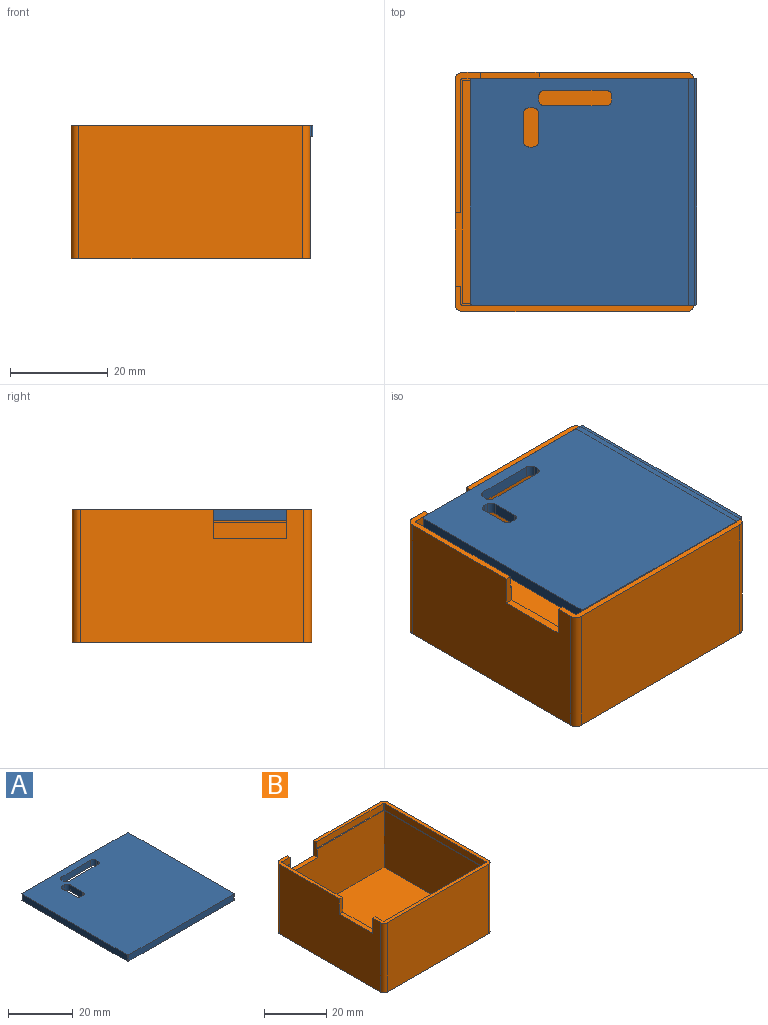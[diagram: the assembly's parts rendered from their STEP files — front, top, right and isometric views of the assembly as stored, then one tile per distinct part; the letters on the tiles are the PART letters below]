
ASSEMBLY  parts=2 mates=1
PART A: 26 faces, bbox 46.4x46.4x2.4 mm
  f0: plane 46.4x46.4mm, normal (0,0,1), area 2081.7mm2, adj f2,f3,f4,f5,f6,f7,f8,f9
  f1: plane 46.4x46.4mm, normal (0,0,-1), area 2081.7mm2, adj f2,f3,f4,f5,f6,f7,f8,f9
  f2: plane 45.6x2.4mm, normal (0,1,0), area 109.4mm2, adj f0,f1,f6,f9
  f3: plane 45.6x2.4mm, normal (-1,0,0), area 109.4mm2, adj f0,f1,f6,f7
  f4: plane 45.6x2.4mm, normal (0,-1,0), area 109.4mm2, adj f0,f1,f7,f8
  f5: plane 45.6x2.4mm, normal (1,0,0), area 109.4mm2, adj f0,f1,f8,f9
  f6: cylinder r=0.4mm len=2.4mm, axis (0,0,1), area 1.5mm2, adj f0,f1,f2,f3
  f7: cylinder r=0.4mm len=2.4mm, axis (0,0,-1), area 1.5mm2, adj f0,f1,f3,f4
  f8: cylinder r=0.4mm len=2.4mm, axis (0,0,1), area 1.5mm2, adj f0,f1,f4,f5
  f9: cylinder r=0.4mm len=2.4mm, axis (0,0,-1), area 1.5mm2, adj f0,f1,f2,f5
  f10: plane 12.6x2.4mm, normal (0,-1,0), area 30.2mm2, adj f0,f1,f22,f25
  f11: plane 2.4x0.8mm, normal (1,0,0), area 1.9mm2, adj f0,f1,f22,f23
  f12: plane 12.6x2.4mm, normal (0,1,0), area 30.2mm2, adj f0,f1,f23,f24
  f13: plane 2.4x0.8mm, normal (-1,0,0), area 1.9mm2, adj f0,f1,f24,f25
  f14: plane 2.4x0.8mm, normal (0,-1,0), area 1.9mm2, adj f0,f1,f18,f21
  f15: plane 5.6x2.4mm, normal (1,0,0), area 13.4mm2, adj f0,f1,f18,f19
  f16: plane 2.4x0.8mm, normal (0,1,0), area 1.9mm2, adj f0,f1,f19,f20
  f17: plane 5.6x2.4mm, normal (-1,0,0), area 13.4mm2, adj f0,f1,f20,f21
  f18: cylinder r=1.2mm len=2.4mm, axis (0,0,1), area 4.5mm2, adj f0,f1,f14,f15
  f19: cylinder r=1.2mm len=2.4mm, axis (0,0,-1), area 4.5mm2, adj f0,f1,f15,f16
  f20: cylinder r=1.2mm len=2.4mm, axis (0,0,1), area 4.5mm2, adj f0,f1,f16,f17
  f21: cylinder r=1.2mm len=2.4mm, axis (0,0,-1), area 4.5mm2, adj f0,f1,f14,f17
  f22: cylinder r=1.2mm len=2.4mm, axis (0,0,1), area 4.5mm2, adj f0,f1,f10,f11
  f23: cylinder r=1.2mm len=2.4mm, axis (0,0,-1), area 4.5mm2, adj f0,f1,f11,f12
  f24: cylinder r=1.2mm len=2.4mm, axis (0,0,1), area 4.5mm2, adj f0,f1,f12,f13
  f25: cylinder r=1.2mm len=2.4mm, axis (0,0,-1), area 4.5mm2, adj f0,f1,f10,f13
PART B: 34 faces, bbox 49x49x27.3 mm
  f0: plane 28.8x5.2mm, normal (0,0,1), area 38.8mm2, adj f2,f7,f8,f12,f18,f25,f29,f31
  f1: plane 27.6x4mm, normal (0,0,1), area 12.4mm2, adj f2,f3,f18,f22,f25,f29,f31
  f2: plane 3.6x2.6mm, normal (0,-1,0), area 9.4mm2, adj f0,f1,f29,f31
  f3: plane 45.8x22.3mm, normal (0,-1,0), area 980.5mm2, adj f1,f6,f20,f22,f23,f27,f28,f29
  f4: plane 49x49mm, normal (0,0,1), area 156.1mm2, adj f5,f7,f8,f9,f10,f13,f14,f15
  f5: plane 3.6x2.6mm, normal (1,0,0), area 9.4mm2, adj f4,f6,f24,f32
  f6: plane 46.6x46.6mm, normal (0,0,1), area 50.5mm2, adj f3,f5,f16,f17,f19,f21,f22,f23
  f7: plane 45.8x27.3mm, normal (0,1,0), area 1178.3mm2, adj f0,f4,f11,f12,f15,f27,f28,f29
  f8: plane 45.8x27.3mm, normal (-1,0,0), area 1160.3mm2, adj f0,f4,f11,f12,f13,f24,f25,f26
  f9: plane 45.8x27.3mm, normal (0,-1,0), area 1250.3mm2, adj f4,f11,f13,f14
  f10: plane 45.8x27.3mm, normal (1,0,0), area 1250.3mm2, adj f4,f11,f14,f15
  f11: plane 49x49mm, normal (0,0,-1), area 2398.8mm2, adj f7,f8,f9,f10,f12,f13,f14,f15
  f12: cylinder r=1.6mm len=27.3mm, axis (0,0,1), area 68.6mm2, adj f0,f7,f8,f11
  f13: cylinder r=1.6mm len=27.3mm, axis (0,0,-1), area 68.6mm2, adj f4,f8,f9,f11
  f14: cylinder r=1.6mm len=27.3mm, axis (0,0,1), area 68.6mm2, adj f4,f9,f10,f11
  f15: cylinder r=1.6mm len=27.3mm, axis (0,0,-1), area 68.6mm2, adj f4,f7,f10,f11
  f16: plane 45.8x2.6mm, normal (-1,0,0), area 119.1mm2, adj f4,f6,f30,f33
  f17: plane 30.2x2.6mm, normal (0,-1,0), area 78.5mm2, adj f4,f6,f27,f30
  f18: plane 27.2x2.6mm, normal (1,0,0), area 70.7mm2, adj f0,f1,f25,f31
  f19: plane 45.8x2.6mm, normal (0,1,0), area 119.1mm2, adj f4,f6,f32,f33
  f20: plane 45.8x45.8mm, normal (0,0,1), area 2097.6mm2, adj f3,f21,f22,f23
  f21: plane 45.8x22.3mm, normal (0,1,0), area 1021.3mm2, adj f6,f20,f22,f23
  f22: plane 45.8x22.3mm, normal (1,0,0), area 970.3mm2, adj f1,f3,f6,f20,f21,f24,f25,f26
  f23: plane 45.8x22.3mm, normal (-1,0,0), area 1021.3mm2, adj f3,f6,f20,f21
  f24: plane 6x1.6mm, normal (0,1,0), area 8.6mm2, adj f4,f5,f6,f8,f22,f26
  f25: plane 6x1.6mm, normal (0,-1,0), area 8.6mm2, adj f0,f1,f8,f18,f22,f26
  f26: plane 15x1.6mm, normal (0,0,1), area 24mm2, adj f8,f22,f24,f25
  f27: plane 6x1.6mm, normal (-1,0,0), area 8.6mm2, adj f3,f4,f6,f7,f17,f28
  f28: plane 12x1.6mm, normal (0,0,1), area 19.2mm2, adj f3,f7,f27,f29
  f29: plane 6x1.6mm, normal (1,0,0), area 8.6mm2, adj f0,f1,f2,f3,f7,f28
  f30: cylinder r=0.4mm len=2.6mm, axis (0,0,1), area 1.6mm2, adj f4,f6,f16,f17
  f31: cylinder r=0.4mm len=2.6mm, axis (0,0,-1), area 1.6mm2, adj f0,f1,f2,f18
  f32: cylinder r=0.4mm len=2.6mm, axis (0,0,1), area 1.6mm2, adj f4,f5,f6,f19
  f33: cylinder r=0.4mm len=2.6mm, axis (0,0,-1), area 1.6mm2, adj f4,f6,f16,f19
PLACE A t=(-73.69,-3.17,25)mm
PLACE B at identity fixed
MATE slider B.f20 <-> A.f0  axis (0,0,1) through (-41.84,40.26,2.4)mm
